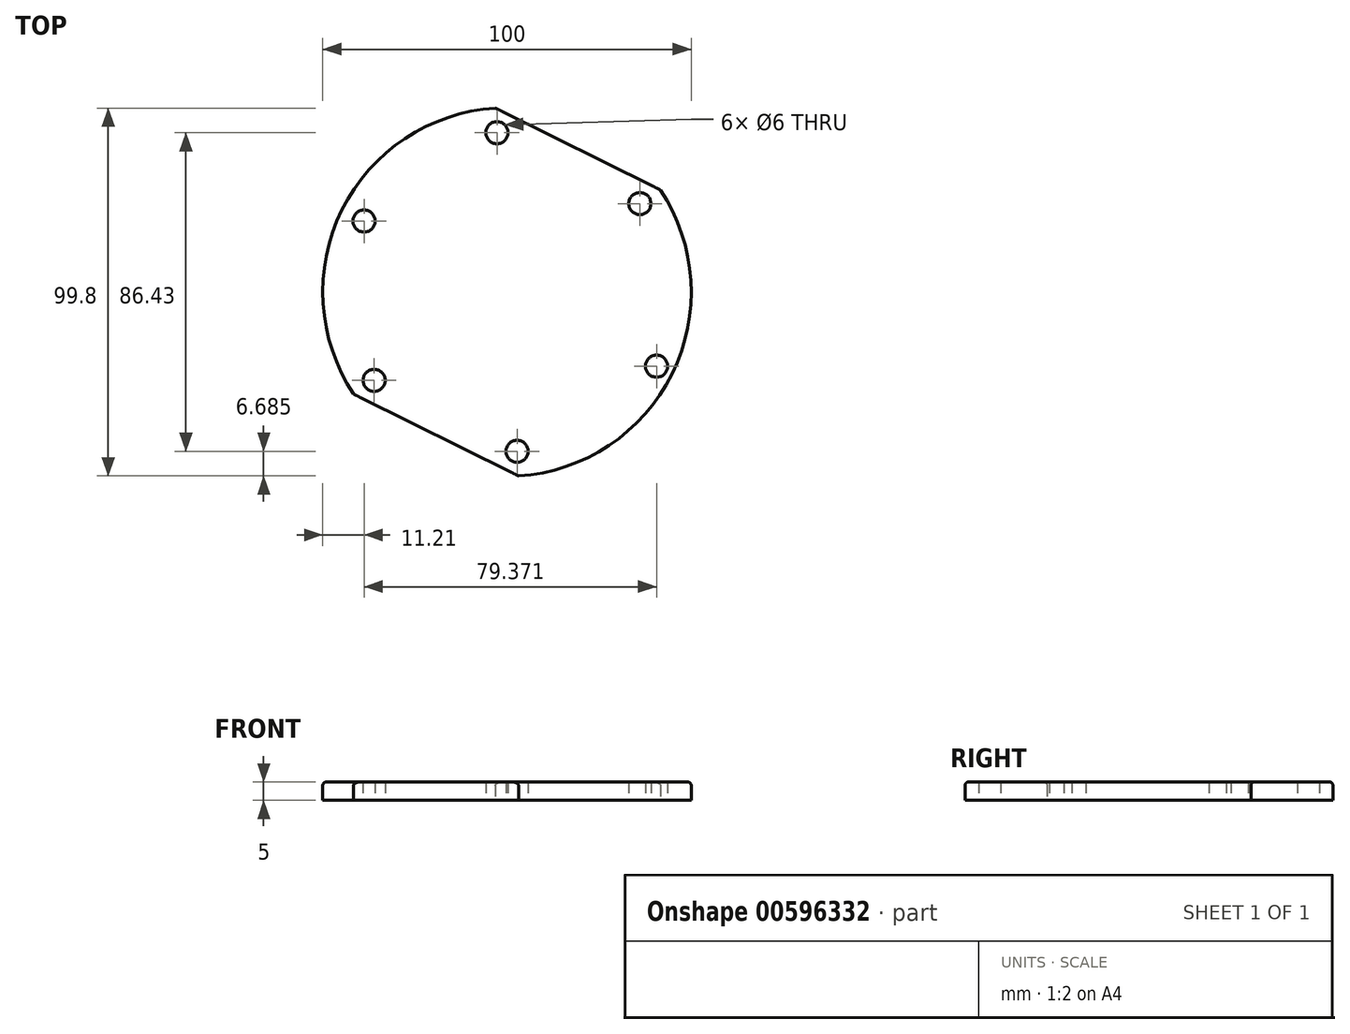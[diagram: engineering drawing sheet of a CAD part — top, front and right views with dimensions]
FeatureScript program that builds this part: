
annotation { "Feature Type Name" : "Feature", "Feature Type Description" : "" }
export const myFeature = defineFeature(function(context is Context, id is Id, definition is map)
    precondition{}
    {
        {
            var Q0;
            Q0=qCreatedBy(makeId("Top.planeOp"),FACE);
            var sketch = newSketch(context, id + "F0", { "sketchPlane" : qUnion([Q0])});
            skArc(sketch, "E0", {"start": v(-3.15, 49.9) * mm, "mid": v(-44.8, 22.22) * mm, "end": v(-41.64, -27.68) * mm});
            skPoint(sketch, "E1.0.midPoint", {"position": v(23.97, -36.06) * mm});
            skLineSegment(sketch, "E2", {"start": v(-43, 21.33) * mm, "end": v(-41.48, 20.58) * mm});
            skLineSegment(sketch, "E3", {"start": v(41.64, 27.68) * mm, "end": v(38.56, 25.63) * mm});
            skLineSegment(sketch, "E4", {"start": v(3.15, -49.9) * mm, "end": v(2.92, -46.2) * mm});
            skCircle(sketch, "E5", {"center": v(-2.73, 43.22) * mm, "radius": 3 * mm});
            skCircle(sketch, "E6", {"center": v(36.06, 23.97) * mm, "radius": 3 * mm});
            skCircle(sketch, "E7", {"center": v(40.58, -20.13) * mm, "radius": 3 * mm});
            skCircle(sketch, "E8", {"center": v(2.73, -43.22) * mm, "radius": 3 * mm});
            skCircle(sketch, "E9", {"center": v(-36.06, -23.97) * mm, "radius": 3 * mm});
            skCircle(sketch, "E10", {"center": v(-38.79, 19.24) * mm, "radius": 3 * mm});
            skLineSegment(sketch, "E11.trimOffspring", {"start": v(-2.92, 46.2) * mm, "end": v(-3.15, 49.9) * mm});
            skLineSegment(sketch, "E12.trimOffspring", {"start": v(-38.56, -25.63) * mm, "end": v(-41.64, -27.68) * mm});
            skLineSegment(sketch, "E13.trimOffspring", {"start": v(43.27, -21.47) * mm, "end": v(44.8, -22.22) * mm});
            skLineSegment(sketch, "E14", {"start": v(-41.64, -27.68) * mm, "end": v(3.15, -49.9) * mm});
            skLineSegment(sketch, "E15", {"start": v(-3.15, 49.9) * mm, "end": v(41.64, 27.68) * mm});
            skArc(sketch, "E16.trimOffspring", {"start": v(3.15, -49.9) * mm, "mid": v(44.8, -22.22) * mm, "end": v(41.64, 27.68) * mm});
            skSolve(sketch);
        }
        {
            var Q0;
            Q0=makeQuery(id+"F0.imprint","IMPRINT",FACE,{"disambiguationData":[TD([[makeQuery(id+"F0.imprint","IMPRINT",EDGE,{"derivedFrom":sQuery(id+"F0.wireOp",EDGE,"E5")}),-1.0]])]});
            extrude(context, id + "F1", {"entities" : qUnion([Q0]), "depth" : 5 * mm, "offsetDistance" : 25 * mm});
        }
        {
            var Q0;
            Q0=makeQuery(id+"F1.opExtrude","CAP_EDGE",EDGE,{"disambiguationData":[OSD([sQuery(id+"F0.wireOp",EDGE,"E0")])],"isStart":false});
            var Q1;
            Q1=makeQuery(id+"F1.opExtrude","CAP_EDGE",EDGE,{"disambiguationData":[OSD([sQuery(id+"F0.wireOp",EDGE,"E16.trimOffspring")])],"isStart":false});
            fillet(context, id + "F2", {"entities" : qUnion([Q0, Q1]), "radius" : 1 * mm, "tangentPropagation" : true, "allowEdgeOverflow" : false});
        }
    });
